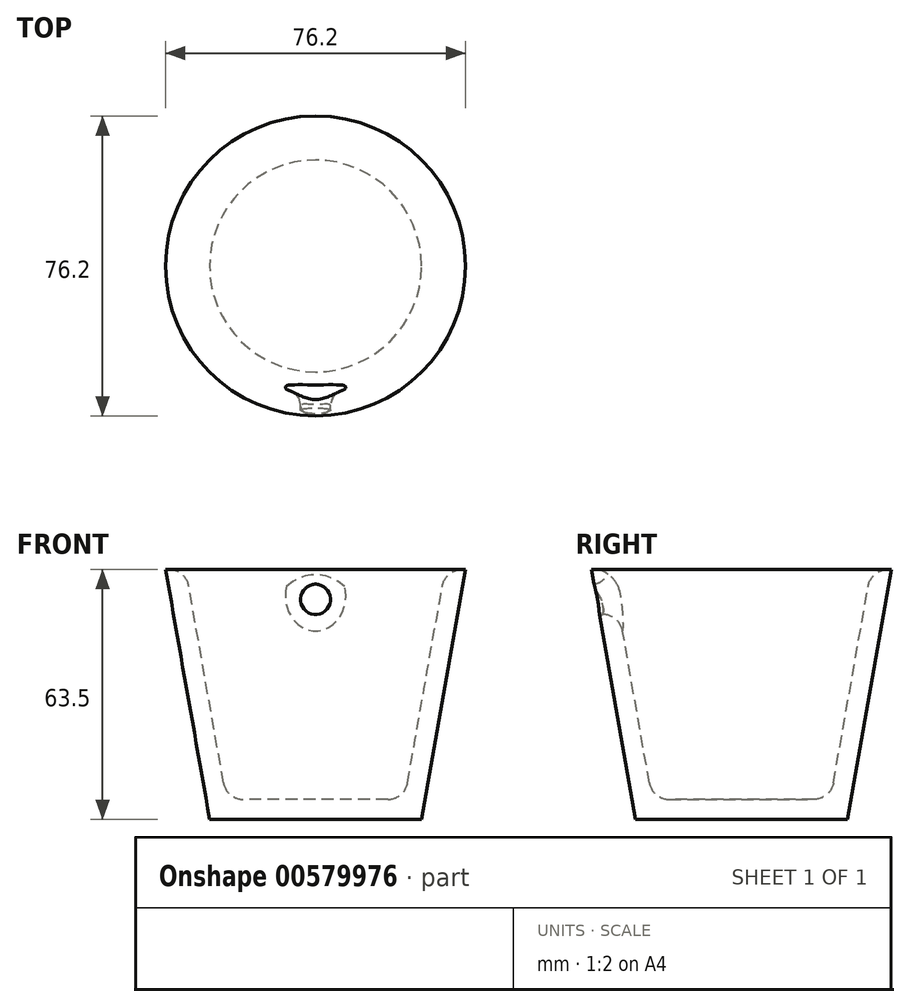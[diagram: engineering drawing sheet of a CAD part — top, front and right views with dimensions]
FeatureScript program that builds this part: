
annotation { "Feature Type Name" : "Feature", "Feature Type Description" : "" }
export const myFeature = defineFeature(function(context is Context, id is Id, definition is map)
    precondition{}
    {
        {
            var Q0;
            Q0=qCreatedBy(makeId("Front.planeOp"),FACE);
            var sketch = newSketch(context, id + "F0", { "sketchPlane" : qUnion([Q0])});
            skLineSegment(sketch, "E0", {"start": v(0, 63.5) * mm, "end": v(-38.1, 63.5) * mm});
            skLineSegment(sketch, "E1", {"start": v(-38.1, 63.5) * mm, "end": v(-26.9, 0) * mm});
            skLineSegment(sketch, "E2", {"start": v(-26.9, 0) * mm, "end": v(0, 0) * mm});
            skLineSegment(sketch, "E3", {"start": v(0, 0) * mm, "end": v(0, 63.5) * mm});
            skSolve(sketch);
        }
        {
            var Q0;
            Q0=makeQuery(id+"F0.imprint","IMPRINT",FACE,{"disambiguationData":[TD([[makeQuery(id+"F0.imprint","IMPRINT",EDGE,{"derivedFrom":sQuery(id+"F0.wireOp",EDGE,"E0")}),1.0]])]});
            var Q1;
            Q1=sQuery(id+"F0.wireOp",EDGE,"E3");
            revolve(context, id + "F1", {"entities" : qUnion([Q0]), "axis" : qUnion([Q1]), "revolveType" : RevolveType.FULL});
        }
        {
            var Q0;
            Q0=makeQuery(id+"F1.opRevolve","SWEPT_FACE",FACE,{"disambiguationData":[OSD([sQuery(id+"F0.wireOp",EDGE,"E0")])]});
            shell(context, id + "F2", {"entities" : qUnion([Q0]), "thickness" : 5.08 * mm});
        }
        {
            var Q0;
            Q0=qCreatedBy(makeId("Front.planeOp"),FACE);
            var sketch = newSketch(context, id + "F3", { "sketchPlane" : qUnion([Q0])});
            skCircle(sketch, "E4", {"center": v(0, 55.88) * mm, "radius": 3.8 * mm});
            skLineSegment(sketch, "E5", {"start": v(0, 63.5) * mm, "end": v(0, 0) * mm});
            skSolve(sketch);
        }
        {
            var Q0;
            Q0 = qSketchRegion(id + "F3", true);
            extrude(context, id + "F4", {"entities" : qUnion([Q0]), "operationType" : NewBodyOperationType.REMOVE, "endBound" : BoundingType.THROUGH_ALL, "depth" : 25.4 * mm, "offsetDistance" : 25.4 * mm});
        }
        {
            var Q0;
            Q0=makeQuery(id+"F2.opShell","OFFSET_FACE",FACE,{"disambiguationData":[OSD([sQuery(id+"F0.wireOp",EDGE,"E1")])]});
            fillet(context, id + "F5", {"entities" : qUnion([Q0]), "radius" : 5.08 * mm, "tangentPropagation" : true, "allowEdgeOverflow" : false});
        }
    });
